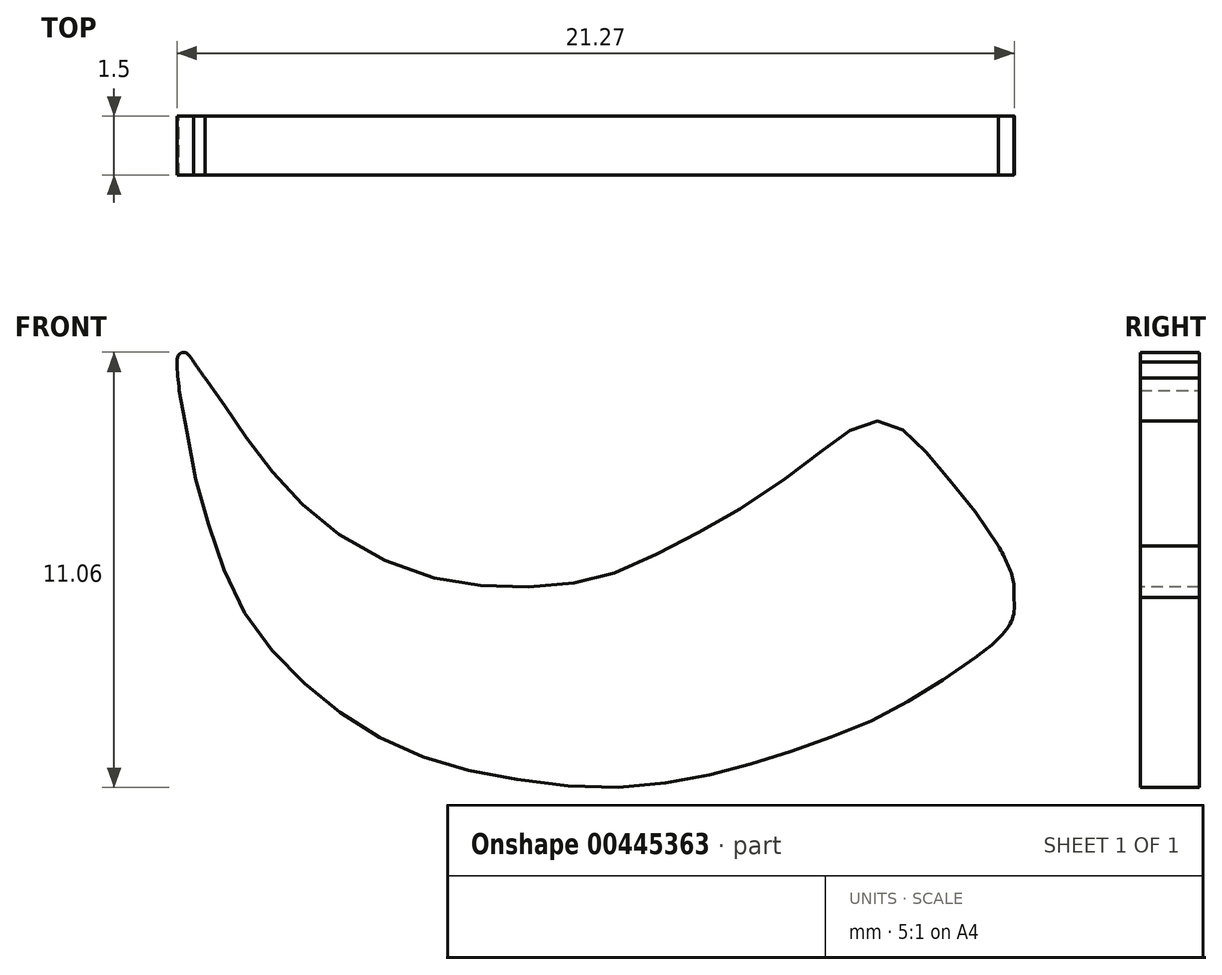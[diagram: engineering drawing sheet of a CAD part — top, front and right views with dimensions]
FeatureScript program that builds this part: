
annotation { "Feature Type Name" : "Feature", "Feature Type Description" : "" }
export const myFeature = defineFeature(function(context is Context, id is Id, definition is map)
    precondition{}
    {
        {
            var Q0;
            Q0=qCreatedBy(makeId("Front.planeOp"),FACE);
            var sketch = newSketch(context, id + "F0", { "sketchPlane" : qUnion([Q0])});
            skFitSpline(sketch, "E0", {"points": [v(-15.59, 11.48) * mm, v(-15.05, 10.72) * mm, v(-14.34, 9.68) * mm, v(-13.38, 8.54) * mm, v(-12.05, 7.4) * mm, v(-10.07, 6.47) * mm, v(-8.28, 6.18) * mm, v(-6.52, 6.22) * mm, v(-5.17, 6.54) * mm, v(-3.58, 7.27) * mm, v(-2.05, 8.12) * mm, v(-0.24, 9.36) * mm, v(0.62, 10.03) * mm, v(1.27, 10.34) * mm, v(1.85, 10.33) * mm, v(2.41, 9.92) * mm, v(3.01, 9.27) * mm, v(3.8, 8.3) * mm, v(4.57, 7.21) * mm, v(4.94, 6.01) * mm, v(4.88, 5.26) * mm, v(4.02, 4.4) * mm, v(2.71, 3.52) * mm, v(1.36, 2.77) * mm, v(-0.23, 2.15) * mm, v(-1.78, 1.65) * mm, v(-3.47, 1.25) * mm, v(-5.51, 1.07) * mm, v(-7.89, 1.31) * mm, v(-9.97, 1.82) * mm, v(-11.78, 2.72) * mm, v(-13.3, 3.95) * mm, v(-14.56, 5.47) * mm, v(-15.38, 7.38) * mm, v(-15.92, 9.38) * mm, v(-16.24, 11.16) * mm, v(-16.37, 11.97) * mm, v(-16.13, 12.23) * mm, v(-15.81, 12.1) * mm], "startDerivative": vector(24.59, -34.02) * mm, "endDerivative": vector(24.8, -17.03) * mm});
            skFitSpline(sketch, "E1", {"points": [v(-16.24, 11.16) * mm, v(-16.3, 11.86) * mm, v(-16.24, 12.08) * mm, v(-16.09, 12.12) * mm, v(-15.87, 11.88) * mm], "startDerivative": vector(-0.24, 2.14) * mm, "endDerivative": vector(0.8, -1.26) * mm});
            skFitSpline(sketch, "E2", {"points": [v(-15.87, 11.88) * mm, v(-15.76, 11.7) * mm, v(-15.59, 11.48) * mm], "startDerivative": vector(0.24, -0.36) * mm, "endDerivative": vector(0.32, -0.44) * mm});
            skFitSpline(sketch, "E3", {"points": [v(4.02, 4.4) * mm, v(4.55, 4.9) * mm, v(4.9, 5.61) * mm, v(4.94, 6.34) * mm, v(4.57, 7.21) * mm], "startDerivative": vector(2.38, 1.92) * mm, "endDerivative": vector(-1.74, 3.22) * mm});
            skSolve(sketch);
        }
        {
            var Q0;
            Q0 = qSketchRegion(id + "F0", true);
            extrude(context, id + "F1", {"entities" : qUnion([Q0]), "depth" : 1.5 * mm});
        }
    });
